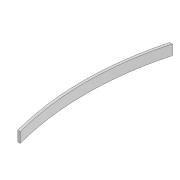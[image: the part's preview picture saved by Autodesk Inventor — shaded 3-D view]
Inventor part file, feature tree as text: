
AUTODESK INVENTOR PART (.ipt)
format: ipt  version: 2022 (Build 260153000, 153)  size: 84,480 bytes
history: native  units: mm
features: extrude x1, sketch x1
ambient origin geometry x8: Origin, YZ Plane, XZ Plane, XY Plane, X Axis, Y Axis, Z Axis, Center Point
bodies: Solid1 (feature_tree)
feature tree (2):
  extrude  "Extrusion1"  Depth=2.0mm
  sketch  "Sketch1"  dims[d0=30.0mm d1=2.0mm d2=2.0mm d3=0.0mm d4=0.5mm d5=0.5mm]
